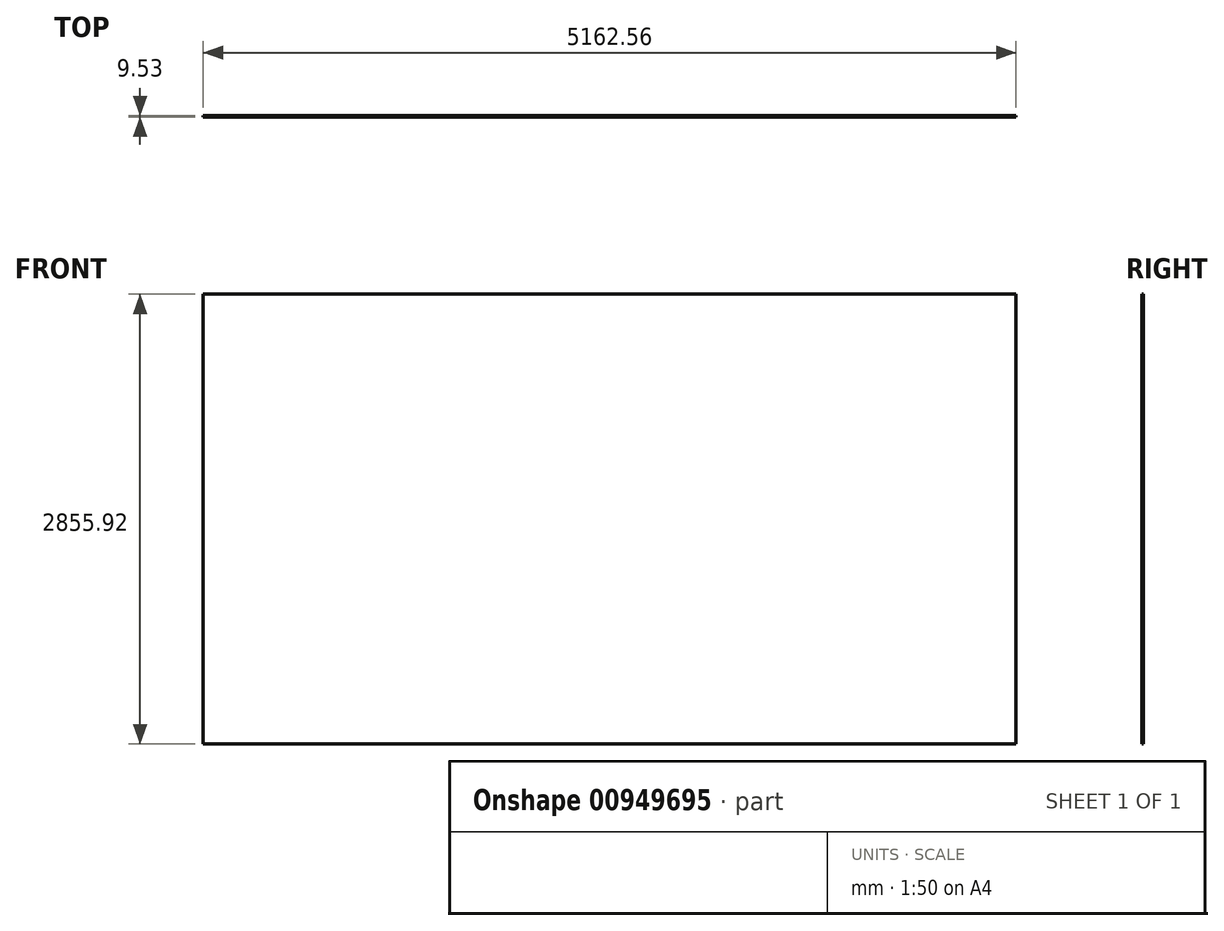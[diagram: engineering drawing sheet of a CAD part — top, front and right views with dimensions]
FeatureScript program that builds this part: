
annotation { "Feature Type Name" : "Feature", "Feature Type Description" : "" }
export const myFeature = defineFeature(function(context is Context, id is Id, definition is map)
    precondition{}
    {
        {
            var Q0;
            Q0=qCreatedBy(makeId("Front.planeOp"),FACE);
            var sketch = newSketch(context, id + "F0", { "sketchPlane" : qUnion([Q0])});
            skLineSegment(sketch, "E0.bottom", {"start": v(-2581.27, -1427.96) * mm, "end": v(2581.28, -1427.96) * mm});
            skLineSegment(sketch, "E0.top", {"start": v(-2581.28, 1427.96) * mm, "end": v(2581.27, 1427.96) * mm});
            skLineSegment(sketch, "E0.left", {"start": v(-2581.27, -1427.96) * mm, "end": v(-2581.28, 1427.96) * mm});
            skLineSegment(sketch, "E0.right", {"start": v(2581.28, -1427.96) * mm, "end": v(2581.27, 1427.96) * mm});
            skPoint(sketch, "E0.middle", {"position": v(0, 0) * mm});
            skSolve(sketch);
        }
        {
            var Q0;
            Q0 = qSketchRegion(id + "F0", true);
            extrude(context, id + "F1", {"entities" : qUnion([Q0]), "depth" : 9.52 * mm, "offsetDistance" : 25.4 * mm});
        }
    });
